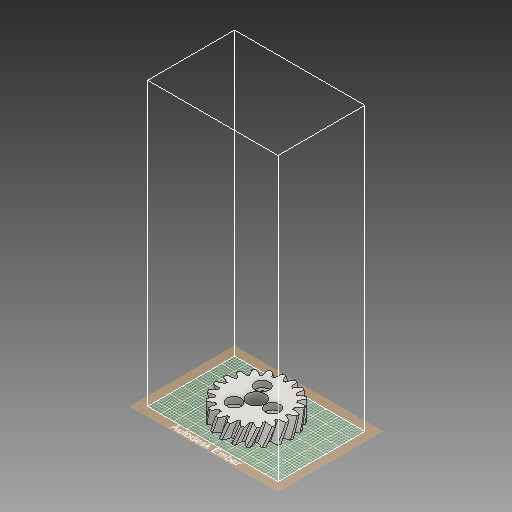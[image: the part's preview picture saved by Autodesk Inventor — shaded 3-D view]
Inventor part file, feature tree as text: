
AUTODESK INVENTOR PART (.ipt)
format: ipt  version: 2017 SP1 (Build 210196100, 196)  size: 839,168 bytes
history: native  units: mm (DEFAULTED — no unit token found)
features: sketch x5, extrude x3, plane x3, other x3, hole x1
ambient origin geometry x8: Origin, YZ Plane, XZ Plane, XY Plane, X Axis, Y Axis, Z Axis, Center Point
bodies: Solid1 (feature_tree)
feature tree (15):
  extrude  "Extrusion1"  Depth=7.0mm TaperAngle=0.0deg
  plane  "Work Plane2"
  plane  "Work Plane8"
  plane  "Work Plane9"
  other  "Engrenage cylindrique"
  extrude  "Extrusion2"  Depth=10.0mm TaperAngle=0.0deg
  hole  "Perçage1"  [1 undecoded]
  extrude  "Extrusion3"  Depth=3.0mm TaperAngle=0.0deg
  sketch  "Sketch1"  dims[d0=32.749068mm d1=7.0mm d2=0.0mm]
  sketch  "Sketch2"  dims[d3=30.066593mm d4=10.0mm d5=0.0mm d16=30.066593mm d17=0.0mm d34=1.570796mm d39=0.0mm d41=0.0mm d43=30.066593mm d46=30.066593mm d47=0.0mm d48=0.0mm d49=8.0mm d50=8.0mm d51=0.0mm d52=15.0mm d53=30.0mm d55=360.0deg d57=3.0mm d58=6.0mm d59=4.0mm d60=2.0mm d61=90.0deg d62=8.0mm d63=20.594885mm d64=6.5mm d65=6.5mm d66=6.5mm d67=3.0mm d68=0.0mm]
  other  "Srf1"
  sketch  "Esquisse3"
  sketch  "Esquisse4"
  sketch  "Esquisse5"
  other  "Diamètre primitif"
note: 1 required parameter value undecoded (feature->parameter linkage not recoverable at this tier; creation-order binding heuristic only, values carry confidence <= 0.55)
